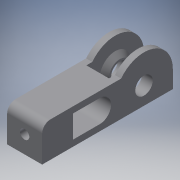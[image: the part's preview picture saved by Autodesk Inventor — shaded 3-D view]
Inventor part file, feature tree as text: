
AUTODESK INVENTOR PART (.ipt)
format: ipt  version: 2018 (Build 220112000, 112)  size: 204,288 bytes
history: native  units: mm
features: extrude x4, sketch x4, projected_geometry x3, fillet x1
ambient origin geometry x8: Origin, YZ Plane, XZ Plane, XY Plane, X Axis, Y Axis, Z Axis, Center Point
bodies: Solid1 (feature_tree)
feature tree (12):
  extrude  "Extrusion1"  Depth=10.0mm TaperAngle=0.0deg
  extrude  "Extrusion2"  Depth=10.0mm TaperAngle=0.0deg
  extrude  "Extrusion3"  Depth=5.0mm TaperAngle=0.0deg
  extrude  "Extrusion4"  [1 undecoded]
  sketch  "Sketch1"  dims[d0=3.0mm d1=10.0mm d2=0.0mm]
  sketch  "Sketch2"  dims[d3=2.0mm d4=10.0mm d5=0.0mm]
  projected_geometry  "Projected Loop1"
  sketch  "Sketch3"  dims[d6=7.0mm d7=0.0mm d8=5.0mm d9=0.0mm]
  projected_geometry  "Projected Loop2"
  sketch  "Sketch4"
  projected_geometry  "Projected Loop3"
  fillet  "Congé1"  [1 undecoded]
note: 2 required parameter values undecoded (feature->parameter linkage not recoverable at this tier; creation-order binding heuristic only, values carry confidence <= 0.55)
